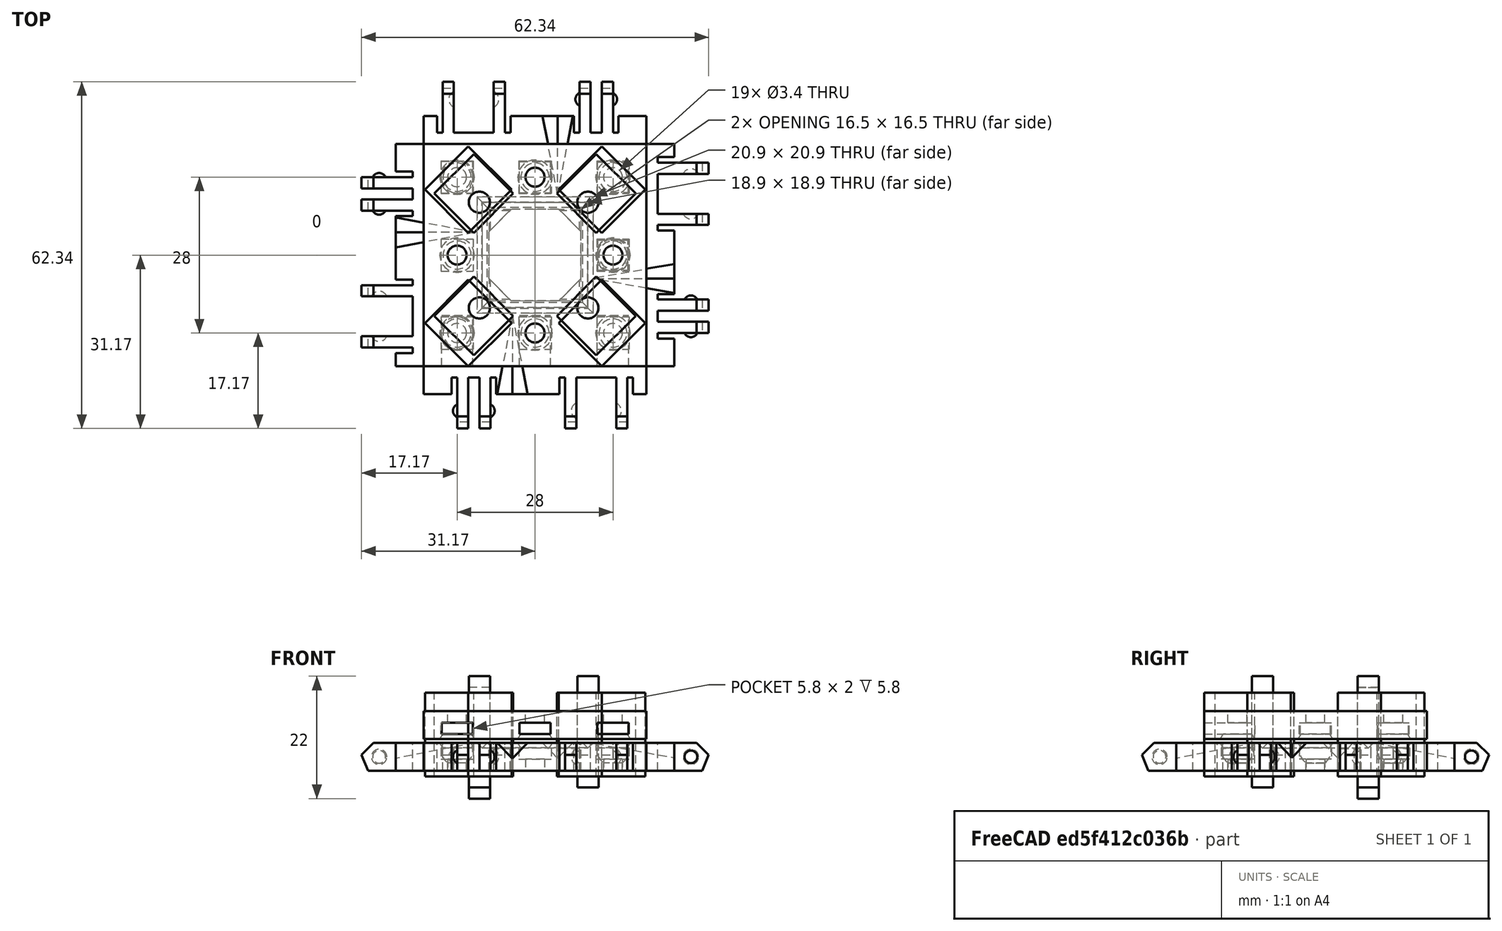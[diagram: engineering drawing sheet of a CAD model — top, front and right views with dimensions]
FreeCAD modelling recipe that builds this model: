
FCSTD DOCUMENT  (FreeCAD 0.17R13522 (Git))
Label: Robot Plates 0.4
License: All rights reserved
LicenseURL: http://en.wikipedia.org/wiki/All_rights_reserved
objects: Part::Box×147, Part::Sphere×51, Part::MultiFuse×49, Part::Cut×48, Part::Cylinder×27, Part::Chamfer×12, Part::Mirroring×2, Part::Fuse×2, App::DocumentObjectGroup×1, Drawing::FeatureViewAnnotation×1, Drawing::FeaturePage×1
note: 338 computed .brp shape members not serialized (recipe doc carries the construction recipe); baked Part::Feature solids carry a one-line shape summary decoded from their .brp

FEATURE [Part::Box] Box  label="Cube"
  AttacherType = Attacher::AttachEngine3D
  Height = 5
  Length = 40
  Placement = pos=(0,0,-2) rot=(0,0,1;0rad)
  Width = 40
FEATURE [Part::Sphere] Sphere003  label="Mag Hole 3"
  Angle1 = -90
  Angle2 = 90
  Angle3 = 360
  AttacherType = Attacher::AttachEngine3D
  Placement = pos=(6,34,1.7) rot=(0,0,1;0rad)
  Radius = 2.85
FEATURE [Part::Sphere] Sphere005  label="Mag Hole 2"
  Angle1 = -90
  Angle2 = 90
  Angle3 = 360
  AttacherType = Attacher::AttachEngine3D
  Placement = pos=(34,20,1.7) rot=(0,0,1;0rad)
  Radius = 2.85
FEATURE [Part::Sphere] Sphere  label="Mag Hole"
  Angle1 = -90
  Angle2 = 90
  Angle3 = 360
  AttacherType = Attacher::AttachEngine3D
  Placement = pos=(6,6,1.7) rot=(0,0,1;0rad)
  Radius = 2.85
FEATURE [Part::MultiFuse] Fusion004
  Shapes = -> [Sphere,Sphere005,Sphere003]
FEATURE [Part::Cut] Cut003
  Base = -> Box
  Tool = -> Fusion004
FEATURE [Part::Box] Box001  label="Cube001"
  AttacherType = Attacher::AttachEngine3D
  Height = 7
  Length = 5
  Width = 40
FEATURE [Part::Box] Box002  label="Cube002"
  AttacherType = Attacher::AttachEngine3D
  Height = 7
  Length = 10
  Placement = pos=(-10,6,0) rot=(0,0,1;0rad)
  Width = 2
FEATURE [Part::Box] Box003  label="Cube003"
  AttacherType = Attacher::AttachEngine3D
  Height = 7
  Length = 10
  Placement = pos=(-10,10,0) rot=(0,0,1;0rad)
  Width = 2
FEATURE [Part::Box] Box004  label="Cube004"
  AttacherType = Attacher::AttachEngine3D
  Height = 7
  Length = 10
  Placement = pos=(-10,25.4,0) rot=(0,0,1;0rad)
  Width = 2
FEATURE [Part::Box] Box005  label="Cube005"
  AttacherType = Attacher::AttachEngine3D
  Height = 7
  Length = 10
  Placement = pos=(-10,34.6,0) rot=(0,0,1;0rad)
  Width = 2
FEATURE [Part::Sphere] Sphere008
  Angle1 = -90
  Angle2 = 90
  Angle3 = 360
  AttacherType = Attacher::AttachEngine3D
  Placement = pos=(-3,6.5,2.5) rot=(0,0,1;0rad)
  Radius = 1.25
FEATURE [Part::Box] Box006  label="Cube006"
  AttacherType = Attacher::AttachEngine3D
  Height = 10
  Length = 13
  Placement = pos=(-10.19,0,-1.19) rot=(0,-1,0;0.785398rad)
  Width = 40
FEATURE [Part::Sphere] Sphere009
  Angle1 = -90
  Angle2 = 90
  Angle3 = 360
  AttacherType = Attacher::AttachEngine3D
  Placement = pos=(-3,11.5,2.5) rot=(0,0,1;0rad)
  Radius = 1.25
FEATURE [Part::Sphere] Sphere010
  Angle1 = -90
  Angle2 = 90
  Angle3 = 360
  AttacherType = Attacher::AttachEngine3D
  Placement = pos=(-3,28,2.5) rot=(0,0,1;0rad)
  Radius = 1.5
FEATURE [Part::Sphere] Sphere011
  Angle1 = -90
  Angle2 = 90
  Angle3 = 360
  AttacherType = Attacher::AttachEngine3D
  Placement = pos=(-3,34,2.5) rot=(0,0,1;0rad)
  Radius = 1.5
FEATURE [Part::MultiFuse] Fusion
  Shapes = -> [Box001,Box002,Box003,Box004,Box005]
FEATURE [Part::Cut] Cut
  Base = -> Fusion
  Tool = -> Box006
FEATURE [Part::MultiFuse] Fusion001
  Shapes = -> [Sphere008,Sphere009,Cut]
FEATURE [Part::MultiFuse] Fusion002
  Shapes = -> [Sphere011,Sphere010]
FEATURE [Part::Cut] Cut001
  Base = -> Fusion001
  Tool = -> Fusion002
FEATURE [Part::Chamfer] Chamfer001
  Base = -> Cut001
  Edges = 4 edges r=4: [Edge31,Edge37,Edge43,Edge46]
FEATURE [Part::Box] Box007  label="Cube007"
  AttacherType = Attacher::AttachEngine3D
  Height = 7
  Length = 4
  Placement = pos=(-1,5,0) rot=(0,0,1;0rad)
  Width = 1
FEATURE [Part::Box] Box008  label="Cube008"
  AttacherType = Attacher::AttachEngine3D
  Height = 7
  Length = 4
  Placement = pos=(-1,8,0) rot=(0,0,1;0rad)
  Width = 2
FEATURE [Part::Box] Box009  label="Cube009"
  AttacherType = Attacher::AttachEngine3D
  Height = 7
  Length = 4
  Placement = pos=(-1,12,0) rot=(0,0,1;0rad)
  Width = 1
FEATURE [Part::Box] Box010  label="Cube010"
  AttacherType = Attacher::AttachEngine3D
  Height = 7
  Length = 4
  Placement = pos=(-1,24.4,0) rot=(0,0,1;0rad)
  Width = 1
FEATURE [Part::Box] Box011  label="Cube011"
  AttacherType = Attacher::AttachEngine3D
  Height = 7
  Length = 4
  Placement = pos=(-1,36.6,0) rot=(0,0,1;0rad)
  Width = 1
FEATURE [Part::Box] Box012  label="Cube012"
  AttacherType = Attacher::AttachEngine3D
  Height = 7
  Length = 4
  Placement = pos=(-1,27.4,0) rot=(0,0,1;0rad)
  Width = 7.2
FEATURE [Part::MultiFuse] Fusion003
  Shapes = -> [Box012,Box009,Box011,Box008,Box010,Box007]
FEATURE [Part::Cut] Cut002
  Base = -> Chamfer001
  Placement = pos=(-5,40,3) rot=(1,0,0;3.14159rad)
  Tool = -> Fusion003
FEATURE [Part::Box] Box013  label="Cube013"
  AttacherType = Attacher::AttachEngine3D
  Height = 10
  Length = 12
  Placement = pos=(-11,-2,-12) rot=(0,0,1;0rad)
  Width = 44
FEATURE [Part::Cut] Cut004
  Base = -> Cut002
  Tool = -> Box013
FEATURE [Part::Box] Box014  label="Cube014"
  AttacherType = Attacher::AttachEngine3D
  Height = 7
  Length = 10
  Placement = pos=(-10,34.6,0) rot=(0,0,1;0rad)
  Width = 2
FEATURE [Part::Box] Box015  label="Cube015"
  AttacherType = Attacher::AttachEngine3D
  Height = 7
  Length = 5
  Width = 40
FEATURE [Part::Box] Box016  label="Cube016"
  AttacherType = Attacher::AttachEngine3D
  Height = 7
  Length = 10
  Placement = pos=(-10,25.4,0) rot=(0,0,1;0rad)
  Width = 2
FEATURE [Part::Box] Box017  label="Cube017"
  AttacherType = Attacher::AttachEngine3D
  Height = 7
  Length = 10
  Placement = pos=(-10,10,0) rot=(0,0,1;0rad)
  Width = 2
FEATURE [Part::Box] Box018  label="Cube018"
  AttacherType = Attacher::AttachEngine3D
  Height = 7
  Length = 10
  Placement = pos=(-10,6,0) rot=(0,0,1;0rad)
  Width = 2
FEATURE [Part::Sphere] Sphere012
  Angle1 = -90
  Angle2 = 90
  Angle3 = 360
  AttacherType = Attacher::AttachEngine3D
  Placement = pos=(-3,6.5,2.5) rot=(0,0,1;0rad)
  Radius = 1.25
FEATURE [Part::Box] Box019  label="Cube019"
  AttacherType = Attacher::AttachEngine3D
  Height = 10
  Length = 13
  Placement = pos=(-10.19,0,-1.19) rot=(0,-1,0;0.785398rad)
  Width = 40
FEATURE [Part::Sphere] Sphere013
  Angle1 = -90
  Angle2 = 90
  Angle3 = 360
  AttacherType = Attacher::AttachEngine3D
  Placement = pos=(-3,11.5,2.5) rot=(0,0,1;0rad)
  Radius = 1.25
FEATURE [Part::Sphere] Sphere014
  Angle1 = -90
  Angle2 = 90
  Angle3 = 360
  AttacherType = Attacher::AttachEngine3D
  Placement = pos=(-3,28,2.5) rot=(0,0,1;0rad)
  Radius = 1.5
FEATURE [Part::Sphere] Sphere015
  Angle1 = -90
  Angle2 = 90
  Angle3 = 360
  AttacherType = Attacher::AttachEngine3D
  Placement = pos=(-3,34,2.5) rot=(0,0,1;0rad)
  Radius = 1.5
FEATURE [Part::MultiFuse] Fusion005
  Shapes = -> [Box015,Box018,Box017,Box016,Box014]
FEATURE [Part::Cut] Cut005
  Base = -> Fusion005
  Tool = -> Box019
FEATURE [Part::MultiFuse] Fusion006
  Shapes = -> [Sphere012,Sphere013,Cut005]
FEATURE [Part::MultiFuse] Fusion007
  Shapes = -> [Sphere015,Sphere014]
FEATURE [Part::Cut] Cut006
  Base = -> Fusion006
  Tool = -> Fusion007
FEATURE [Part::Chamfer] Chamfer002
  Base = -> Cut006
  Edges = 4 edges r=4: [Edge31,Edge37,Edge43,Edge46]
FEATURE [Part::Box] Box020  label="Cube020"
  AttacherType = Attacher::AttachEngine3D
  Height = 7
  Length = 4
  Placement = pos=(-1,5,0) rot=(0,0,1;0rad)
  Width = 1
FEATURE [Part::Box] Box021  label="Cube021"
  AttacherType = Attacher::AttachEngine3D
  Height = 7
  Length = 4
  Placement = pos=(-1,8,0) rot=(0,0,1;0rad)
  Width = 2
FEATURE [Part::Box] Box022  label="Cube022"
  AttacherType = Attacher::AttachEngine3D
  Height = 7
  Length = 4
  Placement = pos=(-1,12,0) rot=(0,0,1;0rad)
  Width = 1
FEATURE [Part::Box] Box023  label="Cube023"
  AttacherType = Attacher::AttachEngine3D
  Height = 7
  Length = 4
  Placement = pos=(-1,24.4,0) rot=(0,0,1;0rad)
  Width = 1
FEATURE [Part::Box] Box024  label="Cube024"
  AttacherType = Attacher::AttachEngine3D
  Height = 7
  Length = 4
  Placement = pos=(-1,36.6,0) rot=(0,0,1;0rad)
  Width = 1
FEATURE [Part::Box] Box025  label="Cube025"
  AttacherType = Attacher::AttachEngine3D
  Height = 7
  Length = 4
  Placement = pos=(-1,27.4,0) rot=(0,0,1;0rad)
  Width = 7.2
FEATURE [Part::MultiFuse] Fusion008
  Shapes = -> [Box025,Box022,Box024,Box021,Box023,Box020]
FEATURE [Part::Cut] Cut007
  Base = -> Chamfer002
  Placement = pos=(-5,40,3) rot=(1,0,0;3.14159rad)
  Tool = -> Fusion008
FEATURE [Part::Box] Box026  label="Cube026"
  AttacherType = Attacher::AttachEngine3D
  Height = 10
  Length = 12
  Placement = pos=(-11,-2,-12) rot=(0,0,1;0rad)
  Width = 44
FEATURE [Part::Cut] Cut008
  Base = -> Cut007
  Placement = pos=(40,0,0) rot=(0,0,1;1.5708rad)
  Tool = -> Box026
FEATURE [Part::Box] Box027  label="Cube027"
  AttacherType = Attacher::AttachEngine3D
  Height = 7
  Length = 4
  Placement = pos=(-1,12,0) rot=(0,0,1;0rad)
  Width = 1
FEATURE [Part::Box] Box028  label="Cube028"
  AttacherType = Attacher::AttachEngine3D
  Height = 10
  Length = 13
  Placement = pos=(-10.19,0,-1.19) rot=(0,-1,0;0.785398rad)
  Width = 40
FEATURE [Part::Box] Box029  label="Cube029"
  AttacherType = Attacher::AttachEngine3D
  Height = 7
  Length = 4
  Placement = pos=(-1,27.4,0) rot=(0,0,1;0rad)
  Width = 7.2
FEATURE [Part::Box] Box030  label="Cube030"
  AttacherType = Attacher::AttachEngine3D
  Height = 7
  Length = 4
  Placement = pos=(-1,5,0) rot=(0,0,1;0rad)
  Width = 1
FEATURE [Part::Box] Box031  label="Cube031"
  AttacherType = Attacher::AttachEngine3D
  Height = 7
  Length = 10
  Placement = pos=(-10,6,0) rot=(0,0,1;0rad)
  Width = 2
FEATURE [Part::Box] Box032  label="Cube032"
  AttacherType = Attacher::AttachEngine3D
  Height = 10
  Length = 12
  Placement = pos=(-11,-2,-12) rot=(0,0,1;0rad)
  Width = 44
FEATURE [Part::Sphere] Sphere016
  Angle1 = -90
  Angle2 = 90
  Angle3 = 360
  AttacherType = Attacher::AttachEngine3D
  Placement = pos=(-3,6.5,2.5) rot=(0,0,1;0rad)
  Radius = 1.25
FEATURE [Part::Box] Box033  label="Cube033"
  AttacherType = Attacher::AttachEngine3D
  Height = 7
  Length = 10
  Placement = pos=(-10,25.4,0) rot=(0,0,1;0rad)
  Width = 2
FEATURE [Part::Box] Box034  label="Cube034"
  AttacherType = Attacher::AttachEngine3D
  Height = 7
  Length = 10
  Placement = pos=(-10,10,0) rot=(0,0,1;0rad)
  Width = 2
FEATURE [Part::Sphere] Sphere017
  Angle1 = -90
  Angle2 = 90
  Angle3 = 360
  AttacherType = Attacher::AttachEngine3D
  Placement = pos=(-3,28,2.5) rot=(0,0,1;0rad)
  Radius = 1.5
FEATURE [Part::Sphere] Sphere018
  Angle1 = -90
  Angle2 = 90
  Angle3 = 360
  AttacherType = Attacher::AttachEngine3D
  Placement = pos=(-3,11.5,2.5) rot=(0,0,1;0rad)
  Radius = 1.25
FEATURE [Part::Box] Box035  label="Cube035"
  AttacherType = Attacher::AttachEngine3D
  Height = 7
  Length = 4
  Placement = pos=(-1,36.6,0) rot=(0,0,1;0rad)
  Width = 1
FEATURE [Part::Sphere] Sphere019
  Angle1 = -90
  Angle2 = 90
  Angle3 = 360
  AttacherType = Attacher::AttachEngine3D
  Placement = pos=(-3,34,2.5) rot=(0,0,1;0rad)
  Radius = 1.5
FEATURE [Part::MultiFuse] Fusion011
  Shapes = -> [Sphere019,Sphere017]
FEATURE [Part::Box] Box036  label="Cube036"
  AttacherType = Attacher::AttachEngine3D
  Height = 7
  Length = 4
  Placement = pos=(-1,8,0) rot=(0,0,1;0rad)
  Width = 2
FEATURE [Part::Box] Box037  label="Cube037"
  AttacherType = Attacher::AttachEngine3D
  Height = 7
  Length = 10
  Placement = pos=(-10,34.6,0) rot=(0,0,1;0rad)
  Width = 2
FEATURE [Part::Box] Box038  label="Cube038"
  AttacherType = Attacher::AttachEngine3D
  Height = 7
  Length = 4
  Placement = pos=(-1,24.4,0) rot=(0,0,1;0rad)
  Width = 1
FEATURE [Part::MultiFuse] Fusion009
  Shapes = -> [Box029,Box027,Box035,Box036,Box038,Box030]
FEATURE [Part::Box] Box039  label="Cube039"
  AttacherType = Attacher::AttachEngine3D
  Height = 7
  Length = 5
  Width = 40
FEATURE [Part::MultiFuse] Fusion012
  Shapes = -> [Box039,Box031,Box034,Box033,Box037]
FEATURE [Part::Cut] Cut011
  Base = -> Fusion012
  Tool = -> Box028
FEATURE [Part::MultiFuse] Fusion010
  Shapes = -> [Sphere016,Sphere018,Cut011]
FEATURE [Part::Cut] Cut012
  Base = -> Fusion010
  Tool = -> Fusion011
FEATURE [Part::Chamfer] Chamfer003
  Base = -> Cut012
  Edges = 4 edges r=4: [Edge31,Edge37,Edge43,Edge46]
FEATURE [Part::Cut] Cut010
  Base = -> Chamfer003
  Placement = pos=(-5,40,3) rot=(1,0,0;3.14159rad)
  Tool = -> Fusion009
FEATURE [Part::Cut] Cut009
  Base = -> Cut010
  Placement = pos=(40,40,0) rot=(0,0,1;3.14159rad)
  Tool = -> Box032
FEATURE [Part::Sphere] Sphere020
  Angle1 = -90
  Angle2 = 90
  Angle3 = 360
  AttacherType = Attacher::AttachEngine3D
  Placement = pos=(-3,11.5,2.5) rot=(0,0,1;0rad)
  Radius = 1.25
FEATURE [Part::Box] Box040  label="Cube040"
  AttacherType = Attacher::AttachEngine3D
  Height = 7
  Length = 10
  Placement = pos=(-10,6,0) rot=(0,0,1;0rad)
  Width = 2
FEATURE [Part::Box] Box041  label="Cube041"
  AttacherType = Attacher::AttachEngine3D
  Height = 7
  Length = 4
  Placement = pos=(-1,8,0) rot=(0,0,1;0rad)
  Width = 2
FEATURE [Part::Box] Box042  label="Cube042"
  AttacherType = Attacher::AttachEngine3D
  Height = 7
  Length = 10
  Placement = pos=(-10,10,0) rot=(0,0,1;0rad)
  Width = 2
FEATURE [Part::Box] Box043  label="Cube043"
  AttacherType = Attacher::AttachEngine3D
  Height = 10
  Length = 12
  Placement = pos=(-11,-2,-12) rot=(0,0,1;0rad)
  Width = 44
FEATURE [Part::Box] Box044  label="Cube044"
  AttacherType = Attacher::AttachEngine3D
  Height = 7
  Length = 4
  Placement = pos=(-1,5,0) rot=(0,0,1;0rad)
  Width = 1
FEATURE [Part::Sphere] Sphere021
  Angle1 = -90
  Angle2 = 90
  Angle3 = 360
  AttacherType = Attacher::AttachEngine3D
  Placement = pos=(-3,28,2.5) rot=(0,0,1;0rad)
  Radius = 1.5
FEATURE [Part::Sphere] Sphere022
  Angle1 = -90
  Angle2 = 90
  Angle3 = 360
  AttacherType = Attacher::AttachEngine3D
  Placement = pos=(-3,6.5,2.5) rot=(0,0,1;0rad)
  Radius = 1.25
FEATURE [Part::Sphere] Sphere023
  Angle1 = -90
  Angle2 = 90
  Angle3 = 360
  AttacherType = Attacher::AttachEngine3D
  Placement = pos=(-3,34,2.5) rot=(0,0,1;0rad)
  Radius = 1.5
FEATURE [Part::Box] Box045  label="Cube045"
  AttacherType = Attacher::AttachEngine3D
  Height = 7
  Length = 4
  Placement = pos=(-1,12,0) rot=(0,0,1;0rad)
  Width = 1
FEATURE [Part::Box] Box046  label="Cube046"
  AttacherType = Attacher::AttachEngine3D
  Height = 7
  Length = 5
  Width = 40
FEATURE [Part::Box] Box047  label="Cube047"
  AttacherType = Attacher::AttachEngine3D
  Height = 7
  Length = 4
  Placement = pos=(-1,36.6,0) rot=(0,0,1;0rad)
  Width = 1
FEATURE [Part::Box] Box048  label="Cube048"
  AttacherType = Attacher::AttachEngine3D
  Height = 7
  Length = 4
  Placement = pos=(-1,24.4,0) rot=(0,0,1;0rad)
  Width = 1
FEATURE [Part::Box] Box049  label="Cube049"
  AttacherType = Attacher::AttachEngine3D
  Height = 7
  Length = 10
  Placement = pos=(-10,25.4,0) rot=(0,0,1;0rad)
  Width = 2
FEATURE [Part::Box] Box050  label="Cube050"
  AttacherType = Attacher::AttachEngine3D
  Height = 10
  Length = 13
  Placement = pos=(-10.19,0,-1.19) rot=(0,-1,0;0.785398rad)
  Width = 40
FEATURE [Part::Box] Box051  label="Cube051"
  AttacherType = Attacher::AttachEngine3D
  Height = 7
  Length = 10
  Placement = pos=(-10,34.6,0) rot=(0,0,1;0rad)
  Width = 2
FEATURE [Part::MultiFuse] Fusion015
  Shapes = -> [Box046,Box040,Box042,Box049,Box051]
FEATURE [Part::Cut] Cut013
  Base = -> Fusion015
  Tool = -> Box050
FEATURE [Part::MultiFuse] Fusion013
  Shapes = -> [Sphere022,Sphere020,Cut013]
FEATURE [Part::MultiFuse] Fusion016
  Shapes = -> [Sphere023,Sphere021]
FEATURE [Part::Cut] Cut014
  Base = -> Fusion013
  Tool = -> Fusion016
FEATURE [Part::Chamfer] Chamfer004
  Base = -> Cut014
  Edges = 4 edges r=4: [Edge31,Edge37,Edge43,Edge46]
FEATURE [Part::Box] Box052  label="Cube052"
  AttacherType = Attacher::AttachEngine3D
  Height = 7
  Length = 4
  Placement = pos=(-1,27.4,0) rot=(0,0,1;0rad)
  Width = 7.2
FEATURE [Part::MultiFuse] Fusion014
  Shapes = -> [Box052,Box045,Box047,Box041,Box048,Box044]
FEATURE [Part::Cut] Cut016
  Base = -> Chamfer004
  Placement = pos=(-5,40,3) rot=(1,0,0;3.14159rad)
  Tool = -> Fusion014
FEATURE [Part::Cut] Cut015
  Base = -> Cut016
  Placement = pos=(0,40,0) rot=(0,0,-1;1.5708rad)
  Tool = -> Box043
FEATURE [Part::Box] Box054  label="Cube054"
  AttacherType = Attacher::AttachEngine3D
  Height = 15
  Length = 10
  Placement = pos=(9,2,-3) rot=(0,0,1;0.785398rad)
  Width = 10
FEATURE [Part::Box] Box055  label="Cube055"
  AttacherType = Attacher::AttachEngine3D
  Height = 15
  Length = 10
  Placement = pos=(31,24,-3) rot=(0,0,1;0.785398rad)
  Width = 10
FEATURE [Part::Box] Box056  label="Cube056"
  AttacherType = Attacher::AttachEngine3D
  Height = 15
  Length = 10
  Placement = pos=(31,2,-3) rot=(0,0,1;0.785398rad)
  Width = 10
FEATURE [Part::Box] Box057  label="Cube057"
  AttacherType = Attacher::AttachEngine3D
  Height = 15
  Length = 10
  Placement = pos=(9,24,-3) rot=(0,0,1;0.785398rad)
  Width = 10
FEATURE [Part::MultiFuse] Fusion017
  Shapes = -> [Box054,Box057,Box056,Box055]
FEATURE [Part::Box] Box058  label="Cube058"
  AttacherType = Attacher::AttachEngine3D
  Height = 5
  Length = 40
  Placement = pos=(0,0,3.7) rot=(0,0,1;0rad)
  Width = 40
FEATURE [Part::Box] Box059  label="Square Nut Hole 008"
  AttacherType = Attacher::AttachEngine3D
  Height = 2
  Length = 5.6
  Placement = pos=(17.2,31.2,4.6) rot=(0,0,1;0rad)
  Width = 5.6
FEATURE [Part::Box] Box060  label="Square Nut Hole 009"
  AttacherType = Attacher::AttachEngine3D
  Height = 2
  Length = 5.6
  Placement = pos=(17.2,-0.85,4.6) rot=(0,0,1;0rad)
  Width = 10
FEATURE [Part::Box] Box061  label="Square Nut Hole 010"
  AttacherType = Attacher::AttachEngine3D
  Height = 2
  Length = 5.6
  Placement = pos=(31.2,-0.85,4.6) rot=(0,0,1;0rad)
  Width = 10
FEATURE [Part::Box] Box062  label="Square Nut Hole 011"
  AttacherType = Attacher::AttachEngine3D
  Height = 2
  Length = 5.4
  Placement = pos=(31.3,17.3,4.6) rot=(0,0,1;0rad)
  Width = 5.4
FEATURE [Part::Box] Box063  label="Square Nut Hole 012"
  AttacherType = Attacher::AttachEngine3D
  Height = 2
  Length = 5.7
  Placement = pos=(3.15,31.15,4.6) rot=(0,0,1;0rad)
  Width = 5.7
FEATURE [Part::Box] Box064  label="Square Nut Hole 013"
  AttacherType = Attacher::AttachEngine3D
  Height = 2
  Length = 5.5
  Placement = pos=(31.25,31.25,4.6) rot=(0,0,1;0rad)
  Width = 5.5
FEATURE [Part::Box] Box065  label="Square Nut Hole 014"
  AttacherType = Attacher::AttachEngine3D
  Height = 2
  Length = 5.8
  Placement = pos=(3.1,17.1,4.6) rot=(0,0,1;0rad)
  Width = 5.8
FEATURE [Part::Box] Box066  label="Square Nut Hole 015"
  AttacherType = Attacher::AttachEngine3D
  Height = 2
  Length = 5.6
  Placement = pos=(3.2,-0.85,4.6) rot=(0,0,1;0rad)
  Width = 10
FEATURE [Part::Sphere] Sphere006  label="Nut Clearence1"
  Angle1 = -90
  Angle2 = 90
  Angle3 = 360
  AttacherType = Attacher::AttachEngine3D
  Placement = pos=(6,6,2.4) rot=(0,0,1;0rad)
  Radius = 3.35
FEATURE [Part::Sphere] Sphere024
  Angle1 = -90
  Angle2 = 90
  Angle3 = 360
  AttacherType = Attacher::AttachEngine3D
  Placement = pos=(6,34,2.4) rot=(0,0,1;0rad)
  Radius = 3.35
FEATURE [Part::Sphere] Sphere007
  Angle1 = -90
  Angle2 = 90
  Angle3 = 360
  AttacherType = Attacher::AttachEngine3D
  Placement = pos=(34,20,2.4) rot=(0,0,1;0rad)
  Radius = 3.35
FEATURE [Part::Sphere] Sphere001
  Angle1 = -90
  Angle2 = 90
  Angle3 = 360
  AttacherType = Attacher::AttachEngine3D
  Placement = pos=(34,6,2.4) rot=(0,0,1;0rad)
  Radius = 3.35
FEATURE [Part::Sphere] Sphere025
  Angle1 = -90
  Angle2 = 90
  Angle3 = 360
  AttacherType = Attacher::AttachEngine3D
  Placement = pos=(20,6,2.4) rot=(0,0,1;0rad)
  Radius = 3.35
FEATURE [Part::Sphere] Sphere026
  Angle1 = -90
  Angle2 = 90
  Angle3 = 360
  AttacherType = Attacher::AttachEngine3D
  Placement = pos=(20,34,2.4) rot=(0,0,1;0rad)
  Radius = 3.35
FEATURE [Part::Sphere] Sphere004
  Angle1 = -90
  Angle2 = 90
  Angle3 = 360
  AttacherType = Attacher::AttachEngine3D
  Placement = pos=(6,20,2.4) rot=(0,0,1;0rad)
  Radius = 3.35
FEATURE [Part::Sphere] Sphere002
  Angle1 = -90
  Angle2 = 90
  Angle3 = 360
  AttacherType = Attacher::AttachEngine3D
  Placement = pos=(34,34,2.4) rot=(0,0,1;0rad)
  Radius = 3.35
FEATURE [Part::Cylinder] Cylinder
  Angle = 360
  AttacherType = Attacher::AttachEngine3D
  Height = 10
  Placement = pos=(6,6,0) rot=(0,0,1;0rad)
  Radius = 1.7
FEATURE [Part::Cylinder] Cylinder002
  Angle = 360
  AttacherType = Attacher::AttachEngine3D
  Height = 10
  Placement = pos=(34,6,0) rot=(0,0,1;0rad)
  Radius = 1.7
FEATURE [Part::Cylinder] Cylinder001
  Angle = 360
  AttacherType = Attacher::AttachEngine3D
  Height = 10
  Placement = pos=(20,6,0) rot=(0,0,1;0rad)
  Radius = 1.7
FEATURE [Part::Cylinder] Cylinder003
  Angle = 360
  AttacherType = Attacher::AttachEngine3D
  Height = 10
  Placement = pos=(34,34,0) rot=(0,0,1;0rad)
  Radius = 1.7
FEATURE [Part::Cylinder] Cylinder004
  Angle = 360
  AttacherType = Attacher::AttachEngine3D
  Height = 10
  Placement = pos=(20,34,0) rot=(0,0,1;0rad)
  Radius = 1.7
FEATURE [Part::Cylinder] Cylinder005
  Angle = 360
  AttacherType = Attacher::AttachEngine3D
  Height = 10
  Placement = pos=(6,34,0) rot=(0,0,1;0rad)
  Radius = 1.7
FEATURE [Part::Cylinder] Cylinder006
  Angle = 360
  AttacherType = Attacher::AttachEngine3D
  Height = 10
  Placement = pos=(6,20,0) rot=(0,0,1;0rad)
  Radius = 1.7
FEATURE [Part::Cylinder] Cylinder007
  Angle = 360
  AttacherType = Attacher::AttachEngine3D
  Height = 10
  Placement = pos=(34,20,0) rot=(0,0,1;0rad)
  Radius = 1.7
FEATURE [Part::MultiFuse] Fusion018
  Shapes = -> [Cylinder,Cylinder004,Cylinder007,Cylinder005,Cylinder006,Cylinder001,Cylinder002,Cylinder003]
FEATURE [Part::MultiFuse] Fusion019
  Shapes = -> [Sphere007,Sphere024,Sphere006,Sphere025,Sphere001,Sphere026,Sphere004,Sphere002]
FEATURE [Part::MultiFuse] Fusion020
  Shapes = -> [Box061,Box065,Box062,Box063,Box064,Box066,Box059,Box060]
FEATURE [Part::Cut] Cut017
  Base = -> Box058
  Tool = -> Fusion020
FEATURE [Part::Cut] Cut019
  Base = -> Cut017
  Tool = -> Fusion019
FEATURE [Part::Cut] Cut018
  Base = -> Cut019
  Tool = -> Fusion018
FEATURE [Part::Cylinder] Cylinder008
  Angle = 360
  AttacherType = Attacher::AttachEngine3D
  Height = 20
  Placement = pos=(10,10.5,-5) rot=(0,0,1;0rad)
  Radius = 1.9
FEATURE [Part::Cylinder] Cylinder009
  Angle = 360
  AttacherType = Attacher::AttachEngine3D
  Height = 20
  Placement = pos=(29.5,10.5,-5) rot=(0,0,1;0rad)
  Radius = 1.9
FEATURE [Part::Cylinder] Cylinder010
  Angle = 360
  AttacherType = Attacher::AttachEngine3D
  Height = 20
  Placement = pos=(29.5,29.5,-5) rot=(0,0,1;0rad)
  Radius = 1.9
FEATURE [Part::Cylinder] Cylinder011
  Angle = 360
  AttacherType = Attacher::AttachEngine3D
  Height = 20
  Placement = pos=(10,29.5,-7) rot=(0,0,1;0rad)
  Radius = 1.9
FEATURE [Part::MultiFuse] Fusion021  label="M2 Screw holes"
  Shapes = -> [Cylinder008,Cylinder009,Cylinder011,Cylinder010]
FEATURE [Part::Box] Box067  label="Square Nut Hole 016"
  AttacherType = Attacher::AttachEngine3D
  Height = 2
  Length = 5.8
  Placement = pos=(31.1,17.1,4.6) rot=(0,0,1;0rad)
  Width = 5.8
FEATURE [Part::Box] Box068  label="Square Nut Hole 017"
  AttacherType = Attacher::AttachEngine3D
  Height = 2
  Length = 5.8
  Placement = pos=(17.1,3.1,4.6) rot=(0,0,1;0rad)
  Width = 5.8
FEATURE [Part::Box] Box069  label="Square Nut Hole 018"
  AttacherType = Attacher::AttachEngine3D
  Height = 2
  Length = 5.8
  Placement = pos=(31.1,3.1,4.6) rot=(0,0,1;0rad)
  Width = 5.8
FEATURE [Part::Box] Box070  label="Square Nut Hole 019"
  AttacherType = Attacher::AttachEngine3D
  Height = 2
  Length = 5.8
  Placement = pos=(3.1,3.1,4.6) rot=(0,0,1;0rad)
  Width = 5.8
FEATURE [Part::Box] Box071  label="Square Nut Hole 020"
  AttacherType = Attacher::AttachEngine3D
  Height = 2
  Length = 5.8
  Placement = pos=(3.1,31.1,4.6) rot=(0,0,1;0rad)
  Width = 5.8
FEATURE [Part::Box] Box072  label="Square Nut Hole 021"
  AttacherType = Attacher::AttachEngine3D
  Height = 2
  Length = 5.8
  Placement = pos=(17.1,31.1,4.6) rot=(0,0,1;0rad)
  Width = 5.8
FEATURE [Part::Box] Box073  label="Square Nut Hole 022"
  AttacherType = Attacher::AttachEngine3D
  Height = 2
  Length = 5.8
  Placement = pos=(31.1,31.1,4.6) rot=(0,0,1;0rad)
  Width = 5.8
FEATURE [Part::Box] Box074  label="Square Nut Hole 023"
  AttacherType = Attacher::AttachEngine3D
  Height = 2
  Length = 5.8
  Placement = pos=(3.1,17.1,4.6) rot=(0,0,1;0rad)
  Width = 5.8
FEATURE [Part::Cylinder] Cylinder012
  Angle = 360
  AttacherType = Attacher::AttachEngine3D
  Height = 10
  Placement = pos=(6,6,0) rot=(0,0,1;0rad)
  Radius = 1.7
FEATURE [Part::Cylinder] Cylinder013
  Angle = 360
  AttacherType = Attacher::AttachEngine3D
  Height = 10
  Placement = pos=(34,34,0) rot=(0,0,1;0rad)
  Radius = 1.7
FEATURE [Part::Cylinder] Cylinder014
  Angle = 360
  AttacherType = Attacher::AttachEngine3D
  Height = 10
  Placement = pos=(20,34,0) rot=(0,0,1;0rad)
  Radius = 1.7
FEATURE [Part::Cylinder] Cylinder015
  Angle = 360
  AttacherType = Attacher::AttachEngine3D
  Height = 10
  Placement = pos=(6,34,0) rot=(0,0,1;0rad)
  Radius = 1.7
FEATURE [Part::Cylinder] Cylinder016
  Angle = 360
  AttacherType = Attacher::AttachEngine3D
  Height = 10
  Placement = pos=(6,20,0) rot=(0,0,1;0rad)
  Radius = 1.7
FEATURE [Part::Cylinder] Cylinder017
  Angle = 360
  AttacherType = Attacher::AttachEngine3D
  Height = 10
  Placement = pos=(34,20,0) rot=(0,0,1;0rad)
  Radius = 1.7
FEATURE [Part::Cylinder] Cylinder018
  Angle = 360
  AttacherType = Attacher::AttachEngine3D
  Height = 10
  Placement = pos=(34,6,0) rot=(0,0,1;0rad)
  Radius = 1.7
FEATURE [Part::Cylinder] Cylinder019
  Angle = 360
  AttacherType = Attacher::AttachEngine3D
  Height = 10
  Placement = pos=(20,6,0) rot=(0,0,1;0rad)
  Radius = 1.7
FEATURE [Part::Box] Box075  label="Cube059"
  AttacherType = Attacher::AttachEngine3D
  Height = 5
  Length = 40
  Placement = pos=(0,0,-2) rot=(0,0,1;0rad)
  Width = 40
FEATURE [Part::Sphere] Sphere027
  Angle1 = -90
  Angle2 = 90
  Angle3 = 360
  AttacherType = Attacher::AttachEngine3D
  Placement = pos=(34,20,2.4) rot=(0,0,1;0rad)
  Radius = 3.35
FEATURE [Part::Sphere] Sphere028  label="Nut Clearence002"
  Angle1 = -90
  Angle2 = 90
  Angle3 = 360
  AttacherType = Attacher::AttachEngine3D
  Placement = pos=(6,6,2.4) rot=(0,0,1;0rad)
  Radius = 3.35
FEATURE [Part::Sphere] Sphere029
  Angle1 = -90
  Angle2 = 90
  Angle3 = 360
  AttacherType = Attacher::AttachEngine3D
  Placement = pos=(34,34,2.4) rot=(0,0,1;0rad)
  Radius = 3.35
FEATURE [Part::Sphere] Sphere030
  Angle1 = -90
  Angle2 = 90
  Angle3 = 360
  AttacherType = Attacher::AttachEngine3D
  Placement = pos=(34,6,2.4) rot=(0,0,1;0rad)
  Radius = 3.35
FEATURE [Part::Sphere] Sphere031
  Angle1 = -90
  Angle2 = 90
  Angle3 = 360
  AttacherType = Attacher::AttachEngine3D
  Placement = pos=(20,6,2.4) rot=(0,0,1;0rad)
  Radius = 3.35
FEATURE [Part::Sphere] Sphere032
  Angle1 = -90
  Angle2 = 90
  Angle3 = 360
  AttacherType = Attacher::AttachEngine3D
  Placement = pos=(6,34,2.4) rot=(0,0,1;0rad)
  Radius = 3.35
FEATURE [Part::Sphere] Sphere033
  Angle1 = -90
  Angle2 = 90
  Angle3 = 360
  AttacherType = Attacher::AttachEngine3D
  Placement = pos=(6,20,2.4) rot=(0,0,1;0rad)
  Radius = 3.35
FEATURE [Part::Sphere] Sphere034
  Angle1 = -90
  Angle2 = 90
  Angle3 = 360
  AttacherType = Attacher::AttachEngine3D
  Placement = pos=(20,34,2.4) rot=(0,0,1;0rad)
  Radius = 3.35
FEATURE [Part::Box] Box076  label="Cube060"
  AttacherType = Attacher::AttachEngine3D
  Height = 15
  Length = 16.5
  Placement = pos=(11.75,11.75,-3) rot=(0,0,1;0rad)
  Width = 16.5
FEATURE [Part::Box] Box077  label="Cube061"
  AttacherType = Attacher::AttachEngine3D
  Height = 15
  Length = 11
  Placement = pos=(8,24,-3) rot=(0,0,1;0.785398rad)
  Width = 11
FEATURE [Part::Box] Box078  label="Cube062"
  AttacherType = Attacher::AttachEngine3D
  Height = 15
  Length = 11
  Placement = pos=(8,0,-3) rot=(0,0,1;0.785398rad)
  Width = 11
FEATURE [Part::Box] Box079  label="Cube063"
  AttacherType = Attacher::AttachEngine3D
  Height = 15
  Length = 11
  Placement = pos=(32,0,-3) rot=(0,0,1;0.785398rad)
  Width = 11
FEATURE [Part::Box] Box080  label="Cube064"
  AttacherType = Attacher::AttachEngine3D
  Height = 15
  Length = 11
  Placement = pos=(32,24,-3) rot=(0,0,1;0.785398rad)
  Width = 11
FEATURE [Part::MultiFuse] Fusion022
  Shapes = -> [Box078,Box077,Box079,Box080]
FEATURE [Part::Cylinder] Cylinder020
  Angle = 360
  AttacherType = Attacher::AttachEngine3D
  Height = 20
  Placement = pos=(29.5,10.5,-5) rot=(0,0,1;0rad)
  Radius = 1.9
FEATURE [Part::Cylinder] Cylinder021
  Angle = 360
  AttacherType = Attacher::AttachEngine3D
  Height = 20
  Placement = pos=(10,29.5,-7) rot=(0,0,1;0rad)
  Radius = 1.9
FEATURE [Part::Cylinder] Cylinder022
  Angle = 360
  AttacherType = Attacher::AttachEngine3D
  Height = 20
  Placement = pos=(10,10.5,-5) rot=(0,0,1;0rad)
  Radius = 1.9
FEATURE [Part::Cylinder] Cylinder023
  Angle = 360
  AttacherType = Attacher::AttachEngine3D
  Height = 20
  Placement = pos=(29.5,29.5,-5) rot=(0,0,1;0rad)
  Radius = 1.9
FEATURE [Part::MultiFuse] Fusion023  label="M2 Screw holes001"
  Shapes = -> [Cylinder022,Cylinder020,Cylinder021,Cylinder023]
FEATURE [Part::MultiFuse] Fusion024  label="Square Nut Hole"
  Shapes = -> [Box067,Box073,Box071,Box069,Box068,Box070,Box072,Box074]
FEATURE [Part::MultiFuse] Fusion025  label="Square Nut Screw Holes"
  Shapes = -> [Cylinder012,Cylinder018,Cylinder016,Cylinder015,Cylinder014,Cylinder013,Cylinder017,Cylinder019]
FEATURE [Part::MultiFuse] Fusion026  label="Nut Chamfers"
  Shapes = -> [Sphere027,Sphere028,Sphere029,Sphere031,Sphere032,Sphere033,Sphere034,Sphere030]
FEATURE [App::DocumentObjectGroup] Group  label="Cubes"
  Group = -> [Fusion017,Fusion022]
FEATURE [Part::Box] Box082  label="Cube066"
  AttacherType = Attacher::AttachEngine3D
  Height = 10
  Length = 15
  Placement = pos=(30.8481,15.8,2.86019) rot=(0.974848,0.205904,-0.085288;0.803573rad)
  Width = 10
FEATURE [Part::Box] Box083  label="Cube067"
  AttacherType = Attacher::AttachEngine3D
  Height = 10
  Length = 21
  Placement = pos=(9.5,9.5,2.1) rot=(0,0,1;0rad)
  Width = 21
FEATURE [Part::Box] Box084  label="Cube068"
  AttacherType = Attacher::AttachEngine3D
  Height = 14
  Length = 17
  Placement = pos=(11.5,11.5,0) rot=(0,0,1;0rad)
  Width = 17
FEATURE [Part::Cut] Cut020
  Base = -> Box083
  Tool = -> Box084
FEATURE [Part::Chamfer] Chamfer007
  Base = -> Cut020
  Edges = 8 edges r=0.95: [Edge4,Edge5,Edge14,Edge16,Edge17,Edge18,Edge19,Edge20]
FEATURE [Part::Chamfer] Chamfer008
  Base = -> Box076
  Edges = 4 edges r=4: [Edge1,Edge3,Edge5,Edge7]
FEATURE [Part::Box] Box085  label="Cube069"
  AttacherType = Attacher::AttachEngine3D
  Height = 15
  Length = 16
  Placement = pos=(12,12,-13) rot=(0,0,1;0rad)
  Width = 16
FEATURE [Part::Box] Box086  label="Cube070"
  AttacherType = Attacher::AttachEngine3D
  Height = 10
  Length = 10
  Placement = pos=(17,32.0919,9.95) rot=(-0.225436,0.969773,-0.093378;0.807337rad)
  Width = 15
FEATURE [Part::Box] Box087  label="Cube071"
  AttacherType = Attacher::AttachEngine3D
  Height = 10
  Length = 10
  Placement = pos=(7.9081,17,9.95) rot=(-0.450607,0.280623,0.847469;1.65638rad)
  Width = 15
FEATURE [Part::Box] Box088  label="Cube072"
  AttacherType = Attacher::AttachEngine3D
  Height = 10
  Length = 10
  Placement = pos=(23,7.9081,9.95) rot=(-0.381178,-0.08861,0.920245;3.06822rad)
  Width = 15
FEATURE [Part::MultiFuse] Fusion027
  Shapes = -> [Box086,Box082,Box087,Box088]
FEATURE [Part::MultiFuse] Fusion028
  Shapes = -> [Cut015,Cut004,Cut008,Cut009]
FEATURE [Part::Box] Box089  label="Cube073"
  AttacherType = Attacher::AttachEngine3D
  Height = 10
  Length = 10
  Placement = pos=(17,32.0919,9.95) rot=(-0.225436,0.969773,-0.093378;0.807337rad)
  Width = 15
FEATURE [Part::Box] Box090  label="Cube074"
  AttacherType = Attacher::AttachEngine3D
  Height = 10
  Length = 15
  Placement = pos=(30.8481,15.8,2.86019) rot=(0.974848,0.205904,-0.085288;0.803573rad)
  Width = 10
FEATURE [Part::Box] Box091  label="Cube075"
  AttacherType = Attacher::AttachEngine3D
  Height = 10
  Length = 10
  Placement = pos=(7.9081,17,9.95) rot=(-0.450607,0.280623,0.847469;1.65638rad)
  Width = 15
FEATURE [Part::Box] Box092  label="Cube076"
  AttacherType = Attacher::AttachEngine3D
  Height = 10
  Length = 10
  Placement = pos=(23,7.9081,9.95) rot=(-0.381178,-0.08861,0.920245;3.06822rad)
  Width = 15
FEATURE [Part::Box] Box093  label="Cube077"
  AttacherType = Attacher::AttachEngine3D
  Height = 7
  Length = 5
  Width = 40
FEATURE [Part::Box] Box094  label="Cube078"
  AttacherType = Attacher::AttachEngine3D
  Height = 7
  Length = 10
  Placement = pos=(-10,6,0) rot=(0,0,1;0rad)
  Width = 2
FEATURE [Part::Box] Box095  label="Cube079"
  AttacherType = Attacher::AttachEngine3D
  Height = 7
  Length = 10
  Placement = pos=(-10,10,0) rot=(0,0,1;0rad)
  Width = 2
FEATURE [Part::Box] Box096  label="Cube080"
  AttacherType = Attacher::AttachEngine3D
  Height = 7
  Length = 10
  Placement = pos=(-10,25.4,0) rot=(0,0,1;0rad)
  Width = 2
FEATURE [Part::Box] Box097  label="Cube081"
  AttacherType = Attacher::AttachEngine3D
  Height = 7
  Length = 10
  Placement = pos=(-10,34.6,0) rot=(0,0,1;0rad)
  Width = 2
FEATURE [Part::Sphere] Sphere035
  Angle1 = -90
  Angle2 = 90
  Angle3 = 360
  AttacherType = Attacher::AttachEngine3D
  Placement = pos=(-3,6.5,2.5) rot=(0,0,1;0rad)
  Radius = 1.25
FEATURE [Part::Box] Box098  label="Cube082"
  AttacherType = Attacher::AttachEngine3D
  Height = 10
  Length = 13
  Placement = pos=(-10.19,0,-1.19) rot=(0,-1,0;0.785398rad)
  Width = 40
FEATURE [Part::Sphere] Sphere036
  Angle1 = -90
  Angle2 = 90
  Angle3 = 360
  AttacherType = Attacher::AttachEngine3D
  Placement = pos=(-3,11.5,2.5) rot=(0,0,1;0rad)
  Radius = 1.25
FEATURE [Part::Sphere] Sphere037
  Angle1 = -90
  Angle2 = 90
  Angle3 = 360
  AttacherType = Attacher::AttachEngine3D
  Placement = pos=(-3,28,2.5) rot=(0,0,1;0rad)
  Radius = 1.5
FEATURE [Part::Sphere] Sphere038
  Angle1 = -90
  Angle2 = 90
  Angle3 = 360
  AttacherType = Attacher::AttachEngine3D
  Placement = pos=(-3,34,2.5) rot=(0,0,1;0rad)
  Radius = 1.5
FEATURE [Part::MultiFuse] Fusion030
  Shapes = -> [Box093,Box094,Box095,Box096,Box097]
FEATURE [Part::Cut] Cut025
  Base = -> Fusion030
  Tool = -> Box098
FEATURE [Part::MultiFuse] Fusion031
  Shapes = -> [Sphere035,Sphere036,Cut025]
FEATURE [Part::MultiFuse] Fusion032
  Shapes = -> [Sphere038,Sphere037]
FEATURE [Part::Cut] Cut026
  Base = -> Fusion031
  Tool = -> Fusion032
FEATURE [Part::Chamfer] Chamfer009
  Base = -> Cut026
  Edges = 4 edges r=4: [Edge31,Edge37,Edge43,Edge46]
FEATURE [Part::Box] Box099  label="Cube083"
  AttacherType = Attacher::AttachEngine3D
  Height = 7
  Length = 4
  Placement = pos=(-1,5,0) rot=(0,0,1;0rad)
  Width = 1
FEATURE [Part::Box] Box100  label="Cube084"
  AttacherType = Attacher::AttachEngine3D
  Height = 7
  Length = 4
  Placement = pos=(-1,8,0) rot=(0,0,1;0rad)
  Width = 2
FEATURE [Part::Box] Box101  label="Cube085"
  AttacherType = Attacher::AttachEngine3D
  Height = 7
  Length = 4
  Placement = pos=(-1,12,0) rot=(0,0,1;0rad)
  Width = 1
FEATURE [Part::Box] Box102  label="Cube086"
  AttacherType = Attacher::AttachEngine3D
  Height = 7
  Length = 4
  Placement = pos=(-1,24.4,0) rot=(0,0,1;0rad)
  Width = 1
FEATURE [Part::Box] Box103  label="Cube087"
  AttacherType = Attacher::AttachEngine3D
  Height = 7
  Length = 4
  Placement = pos=(-1,36.6,0) rot=(0,0,1;0rad)
  Width = 1
FEATURE [Part::Box] Box104  label="Cube088"
  AttacherType = Attacher::AttachEngine3D
  Height = 7
  Length = 4
  Placement = pos=(-1,27.4,0) rot=(0,0,1;0rad)
  Width = 7.2
FEATURE [Part::MultiFuse] Fusion033
  Shapes = -> [Box104,Box101,Box103,Box100,Box102,Box099]
FEATURE [Part::Cut] Cut027
  Base = -> Chamfer009
  Placement = pos=(-5,40,3) rot=(1,0,0;3.14159rad)
  Tool = -> Fusion033
FEATURE [Part::Box] Box105  label="Cube089"
  AttacherType = Attacher::AttachEngine3D
  Height = 10
  Length = 12
  Placement = pos=(-11,-2,-12) rot=(0,0,1;0rad)
  Width = 44
FEATURE [Part::Cut] Cut028
  Base = -> Cut027
  Tool = -> Box105
FEATURE [Part::Box] Box106  label="Cube090"
  AttacherType = Attacher::AttachEngine3D
  Height = 7
  Length = 10
  Placement = pos=(-10,34.6,0) rot=(0,0,1;0rad)
  Width = 2
FEATURE [Part::Box] Box107  label="Cube091"
  AttacherType = Attacher::AttachEngine3D
  Height = 7
  Length = 5
  Width = 40
FEATURE [Part::Box] Box108  label="Cube092"
  AttacherType = Attacher::AttachEngine3D
  Height = 7
  Length = 10
  Placement = pos=(-10,25.4,0) rot=(0,0,1;0rad)
  Width = 2
FEATURE [Part::Box] Box109  label="Cube093"
  AttacherType = Attacher::AttachEngine3D
  Height = 7
  Length = 10
  Placement = pos=(-10,10,0) rot=(0,0,1;0rad)
  Width = 2
FEATURE [Part::Box] Box110  label="Cube094"
  AttacherType = Attacher::AttachEngine3D
  Height = 7
  Length = 10
  Placement = pos=(-10,6,0) rot=(0,0,1;0rad)
  Width = 2
FEATURE [Part::Sphere] Sphere039
  Angle1 = -90
  Angle2 = 90
  Angle3 = 360
  AttacherType = Attacher::AttachEngine3D
  Placement = pos=(-3,6.5,2.5) rot=(0,0,1;0rad)
  Radius = 1.25
FEATURE [Part::Box] Box111  label="Cube095"
  AttacherType = Attacher::AttachEngine3D
  Height = 10
  Length = 13
  Placement = pos=(-10.19,0,-1.19) rot=(0,-1,0;0.785398rad)
  Width = 40
FEATURE [Part::Sphere] Sphere040
  Angle1 = -90
  Angle2 = 90
  Angle3 = 360
  AttacherType = Attacher::AttachEngine3D
  Placement = pos=(-3,11.5,2.5) rot=(0,0,1;0rad)
  Radius = 1.25
FEATURE [Part::Sphere] Sphere041
  Angle1 = -90
  Angle2 = 90
  Angle3 = 360
  AttacherType = Attacher::AttachEngine3D
  Placement = pos=(-3,28,2.5) rot=(0,0,1;0rad)
  Radius = 1.5
FEATURE [Part::Sphere] Sphere042
  Angle1 = -90
  Angle2 = 90
  Angle3 = 360
  AttacherType = Attacher::AttachEngine3D
  Placement = pos=(-3,34,2.5) rot=(0,0,1;0rad)
  Radius = 1.5
FEATURE [Part::MultiFuse] Fusion034
  Shapes = -> [Box107,Box110,Box109,Box108,Box106]
FEATURE [Part::Cut] Cut029
  Base = -> Fusion034
  Tool = -> Box111
FEATURE [Part::MultiFuse] Fusion035
  Shapes = -> [Sphere039,Sphere040,Cut029]
FEATURE [Part::MultiFuse] Fusion036
  Shapes = -> [Sphere042,Sphere041]
FEATURE [Part::Cut] Cut030
  Base = -> Fusion035
  Tool = -> Fusion036
FEATURE [Part::Chamfer] Chamfer010
  Base = -> Cut030
  Edges = 4 edges r=4: [Edge31,Edge37,Edge43,Edge46]
FEATURE [Part::Box] Box112  label="Cube096"
  AttacherType = Attacher::AttachEngine3D
  Height = 7
  Length = 4
  Placement = pos=(-1,5,0) rot=(0,0,1;0rad)
  Width = 1
FEATURE [Part::Box] Box113  label="Cube097"
  AttacherType = Attacher::AttachEngine3D
  Height = 7
  Length = 4
  Placement = pos=(-1,8,0) rot=(0,0,1;0rad)
  Width = 2
FEATURE [Part::Box] Box114  label="Cube098"
  AttacherType = Attacher::AttachEngine3D
  Height = 7
  Length = 4
  Placement = pos=(-1,12,0) rot=(0,0,1;0rad)
  Width = 1
FEATURE [Part::Box] Box115  label="Cube099"
  AttacherType = Attacher::AttachEngine3D
  Height = 7
  Length = 4
  Placement = pos=(-1,24.4,0) rot=(0,0,1;0rad)
  Width = 1
FEATURE [Part::Box] Box116  label="Cube100"
  AttacherType = Attacher::AttachEngine3D
  Height = 7
  Length = 4
  Placement = pos=(-1,36.6,0) rot=(0,0,1;0rad)
  Width = 1
FEATURE [Part::Box] Box117  label="Cube101"
  AttacherType = Attacher::AttachEngine3D
  Height = 7
  Length = 4
  Placement = pos=(-1,27.4,0) rot=(0,0,1;0rad)
  Width = 7.2
FEATURE [Part::MultiFuse] Fusion037
  Shapes = -> [Box117,Box114,Box116,Box113,Box115,Box112]
FEATURE [Part::Cut] Cut031
  Base = -> Chamfer010
  Placement = pos=(-5,40,3) rot=(1,0,0;3.14159rad)
  Tool = -> Fusion037
FEATURE [Part::Box] Box118  label="Cube102"
  AttacherType = Attacher::AttachEngine3D
  Height = 10
  Length = 12
  Placement = pos=(-11,-2,-12) rot=(0,0,1;0rad)
  Width = 44
FEATURE [Part::Cut] Cut032
  Base = -> Cut031
  Placement = pos=(40,0,0) rot=(0,0,1;1.5708rad)
  Tool = -> Box118
FEATURE [Part::Box] Box119  label="Cube103"
  AttacherType = Attacher::AttachEngine3D
  Height = 7
  Length = 4
  Placement = pos=(-1,12,0) rot=(0,0,1;0rad)
  Width = 1
FEATURE [Part::Box] Box120  label="Cube104"
  AttacherType = Attacher::AttachEngine3D
  Height = 10
  Length = 13
  Placement = pos=(-10.19,0,-1.19) rot=(0,-1,0;0.785398rad)
  Width = 40
FEATURE [Part::Box] Box121  label="Cube105"
  AttacherType = Attacher::AttachEngine3D
  Height = 7
  Length = 4
  Placement = pos=(-1,27.4,0) rot=(0,0,1;0rad)
  Width = 7.2
FEATURE [Part::Box] Box122  label="Cube106"
  AttacherType = Attacher::AttachEngine3D
  Height = 7
  Length = 4
  Placement = pos=(-1,5,0) rot=(0,0,1;0rad)
  Width = 1
FEATURE [Part::Box] Box123  label="Cube107"
  AttacherType = Attacher::AttachEngine3D
  Height = 7
  Length = 10
  Placement = pos=(-10,6,0) rot=(0,0,1;0rad)
  Width = 2
FEATURE [Part::Box] Box124  label="Cube108"
  AttacherType = Attacher::AttachEngine3D
  Height = 10
  Length = 12
  Placement = pos=(-11,-2,-12) rot=(0,0,1;0rad)
  Width = 44
FEATURE [Part::Sphere] Sphere043
  Angle1 = -90
  Angle2 = 90
  Angle3 = 360
  AttacherType = Attacher::AttachEngine3D
  Placement = pos=(-3,6.5,2.5) rot=(0,0,1;0rad)
  Radius = 1.25
FEATURE [Part::Box] Box125  label="Cube109"
  AttacherType = Attacher::AttachEngine3D
  Height = 7
  Length = 10
  Placement = pos=(-10,25.4,0) rot=(0,0,1;0rad)
  Width = 2
FEATURE [Part::Box] Box126  label="Cube110"
  AttacherType = Attacher::AttachEngine3D
  Height = 7
  Length = 10
  Placement = pos=(-10,10,0) rot=(0,0,1;0rad)
  Width = 2
FEATURE [Part::Sphere] Sphere044
  Angle1 = -90
  Angle2 = 90
  Angle3 = 360
  AttacherType = Attacher::AttachEngine3D
  Placement = pos=(-3,28,2.5) rot=(0,0,1;0rad)
  Radius = 1.5
FEATURE [Part::Sphere] Sphere045
  Angle1 = -90
  Angle2 = 90
  Angle3 = 360
  AttacherType = Attacher::AttachEngine3D
  Placement = pos=(-3,11.5,2.5) rot=(0,0,1;0rad)
  Radius = 1.25
FEATURE [Part::Box] Box127  label="Cube111"
  AttacherType = Attacher::AttachEngine3D
  Height = 7
  Length = 4
  Placement = pos=(-1,36.6,0) rot=(0,0,1;0rad)
  Width = 1
FEATURE [Part::Sphere] Sphere046
  Angle1 = -90
  Angle2 = 90
  Angle3 = 360
  AttacherType = Attacher::AttachEngine3D
  Placement = pos=(-3,34,2.5) rot=(0,0,1;0rad)
  Radius = 1.5
FEATURE [Part::MultiFuse] Fusion040
  Shapes = -> [Sphere046,Sphere044]
FEATURE [Part::Box] Box128  label="Cube112"
  AttacherType = Attacher::AttachEngine3D
  Height = 7
  Length = 4
  Placement = pos=(-1,8,0) rot=(0,0,1;0rad)
  Width = 2
FEATURE [Part::Box] Box129  label="Cube113"
  AttacherType = Attacher::AttachEngine3D
  Height = 7
  Length = 10
  Placement = pos=(-10,34.6,0) rot=(0,0,1;0rad)
  Width = 2
FEATURE [Part::Box] Box130  label="Cube114"
  AttacherType = Attacher::AttachEngine3D
  Height = 7
  Length = 4
  Placement = pos=(-1,24.4,0) rot=(0,0,1;0rad)
  Width = 1
FEATURE [Part::MultiFuse] Fusion038
  Shapes = -> [Box121,Box119,Box127,Box128,Box130,Box122]
FEATURE [Part::Box] Box131  label="Cube115"
  AttacherType = Attacher::AttachEngine3D
  Height = 7
  Length = 5
  Width = 40
FEATURE [Part::MultiFuse] Fusion041
  Shapes = -> [Box131,Box123,Box126,Box125,Box129]
FEATURE [Part::Cut] Cut035
  Base = -> Fusion041
  Tool = -> Box120
FEATURE [Part::MultiFuse] Fusion039
  Shapes = -> [Sphere043,Sphere045,Cut035]
FEATURE [Part::Cut] Cut036
  Base = -> Fusion039
  Tool = -> Fusion040
FEATURE [Part::Chamfer] Chamfer011
  Base = -> Cut036
  Edges = 4 edges r=4: [Edge31,Edge37,Edge43,Edge46]
FEATURE [Part::Cut] Cut034
  Base = -> Chamfer011
  Placement = pos=(-5,40,3) rot=(1,0,0;3.14159rad)
  Tool = -> Fusion038
FEATURE [Part::Cut] Cut033
  Base = -> Cut034
  Placement = pos=(40,40,0) rot=(0,0,1;3.14159rad)
  Tool = -> Box124
FEATURE [Part::Sphere] Sphere047
  Angle1 = -90
  Angle2 = 90
  Angle3 = 360
  AttacherType = Attacher::AttachEngine3D
  Placement = pos=(-3,11.5,2.5) rot=(0,0,1;0rad)
  Radius = 1.25
FEATURE [Part::Box] Box132  label="Cube116"
  AttacherType = Attacher::AttachEngine3D
  Height = 7
  Length = 10
  Placement = pos=(-10,6,0) rot=(0,0,1;0rad)
  Width = 2
FEATURE [Part::Box] Box133  label="Cube117"
  AttacherType = Attacher::AttachEngine3D
  Height = 7
  Length = 4
  Placement = pos=(-1,8,0) rot=(0,0,1;0rad)
  Width = 2
FEATURE [Part::Box] Box134  label="Cube118"
  AttacherType = Attacher::AttachEngine3D
  Height = 7
  Length = 10
  Placement = pos=(-10,10,0) rot=(0,0,1;0rad)
  Width = 2
FEATURE [Part::Box] Box135  label="Cube119"
  AttacherType = Attacher::AttachEngine3D
  Height = 10
  Length = 12
  Placement = pos=(-11,-2,-12) rot=(0,0,1;0rad)
  Width = 44
FEATURE [Part::Box] Box136  label="Cube120"
  AttacherType = Attacher::AttachEngine3D
  Height = 7
  Length = 4
  Placement = pos=(-1,5,0) rot=(0,0,1;0rad)
  Width = 1
FEATURE [Part::Sphere] Sphere048
  Angle1 = -90
  Angle2 = 90
  Angle3 = 360
  AttacherType = Attacher::AttachEngine3D
  Placement = pos=(-3,28,2.5) rot=(0,0,1;0rad)
  Radius = 1.5
FEATURE [Part::Sphere] Sphere049
  Angle1 = -90
  Angle2 = 90
  Angle3 = 360
  AttacherType = Attacher::AttachEngine3D
  Placement = pos=(-3,6.5,2.5) rot=(0,0,1;0rad)
  Radius = 1.25
FEATURE [Part::Sphere] Sphere050
  Angle1 = -90
  Angle2 = 90
  Angle3 = 360
  AttacherType = Attacher::AttachEngine3D
  Placement = pos=(-3,34,2.5) rot=(0,0,1;0rad)
  Radius = 1.5
FEATURE [Part::Box] Box137  label="Cube121"
  AttacherType = Attacher::AttachEngine3D
  Height = 7
  Length = 4
  Placement = pos=(-1,12,0) rot=(0,0,1;0rad)
  Width = 1
FEATURE [Part::Box] Box138  label="Cube122"
  AttacherType = Attacher::AttachEngine3D
  Height = 7
  Length = 5
  Width = 40
FEATURE [Part::Box] Box139  label="Cube123"
  AttacherType = Attacher::AttachEngine3D
  Height = 7
  Length = 4
  Placement = pos=(-1,36.6,0) rot=(0,0,1;0rad)
  Width = 1
FEATURE [Part::Box] Box140  label="Cube124"
  AttacherType = Attacher::AttachEngine3D
  Height = 7
  Length = 4
  Placement = pos=(-1,24.4,0) rot=(0,0,1;0rad)
  Width = 1
FEATURE [Part::Box] Box141  label="Cube125"
  AttacherType = Attacher::AttachEngine3D
  Height = 7
  Length = 10
  Placement = pos=(-10,25.4,0) rot=(0,0,1;0rad)
  Width = 2
FEATURE [Part::Box] Box142  label="Cube126"
  AttacherType = Attacher::AttachEngine3D
  Height = 10
  Length = 13
  Placement = pos=(-10.19,0,-1.19) rot=(0,-1,0;0.785398rad)
  Width = 40
FEATURE [Part::Box] Box143  label="Cube127"
  AttacherType = Attacher::AttachEngine3D
  Height = 7
  Length = 10
  Placement = pos=(-10,34.6,0) rot=(0,0,1;0rad)
  Width = 2
FEATURE [Part::MultiFuse] Fusion044
  Shapes = -> [Box138,Box132,Box134,Box141,Box143]
FEATURE [Part::Cut] Cut037
  Base = -> Fusion044
  Tool = -> Box142
FEATURE [Part::MultiFuse] Fusion042
  Shapes = -> [Sphere049,Sphere047,Cut037]
FEATURE [Part::MultiFuse] Fusion045
  Shapes = -> [Sphere050,Sphere048]
FEATURE [Part::Cut] Cut038
  Base = -> Fusion042
  Tool = -> Fusion045
FEATURE [Part::Chamfer] Chamfer012
  Base = -> Cut038
  Edges = 4 edges r=4: [Edge31,Edge37,Edge43,Edge46]
FEATURE [Part::Box] Box144  label="Cube128"
  AttacherType = Attacher::AttachEngine3D
  Height = 7
  Length = 4
  Placement = pos=(-1,27.4,0) rot=(0,0,1;0rad)
  Width = 7.2
FEATURE [Part::MultiFuse] Fusion043
  Shapes = -> [Box144,Box137,Box139,Box133,Box140,Box136]
FEATURE [Part::Cut] Cut040
  Base = -> Chamfer012
  Placement = pos=(-5,40,3) rot=(1,0,0;3.14159rad)
  Tool = -> Fusion043
FEATURE [Part::Cut] Cut039
  Base = -> Cut040
  Placement = pos=(0,40,0) rot=(0,0,-1;1.5708rad)
  Tool = -> Box135
FEATURE [Part::MultiFuse] Fusion046
  Shapes = -> [Cut039,Cut028,Cut032,Cut033]
FEATURE [Part::MultiFuse] Fusion047
  Placement = pos=(0,40,6.7) rot=(1,0,0;3.14159rad)
  Shapes = -> [Fusion026,Fusion024,Fusion025]
FEATURE [Part::MultiFuse] Fusion048
  Shapes = -> [Box089,Box091,Box090,Box092]
FEATURE [Part::Box] Box145  label="Cube129"
  AttacherType = Attacher::AttachEngine3D
  Height = 15
  Length = 16
  Placement = pos=(12,12,-13) rot=(0,0,1;0rad)
  Width = 16
FEATURE [Part::Box] Box146  label="Cube130"
  AttacherType = Attacher::AttachEngine3D
  Height = 15
  Length = 16.5
  Placement = pos=(11.75,11.75,-3) rot=(0,0,1;0rad)
  Width = 16.5
FEATURE [Part::Chamfer] Chamfer013
  Base = -> Box146
  Edges = 4 edges r=4: [Edge1,Edge3,Edge5,Edge7]
FEATURE [Part::Box] Box147  label="Cube131"
  AttacherType = Attacher::AttachEngine3D
  Height = 10
  Length = 21
  Placement = pos=(9.5,9.5,2.1) rot=(0,0,1;0rad)
  Width = 21
FEATURE [Part::Box] Box148  label="Cube132"
  AttacherType = Attacher::AttachEngine3D
  Height = 14
  Length = 17
  Placement = pos=(11.5,11.5,0) rot=(0,0,1;0rad)
  Width = 17
FEATURE [Part::Cut] Cut043
  Base = -> Box147
  Tool = -> Box148
FEATURE [Part::Chamfer] Chamfer014
  Base = -> Cut043
  Edges = 8 edges r=0.95: [Edge4,Edge5,Edge14,Edge16,Edge17,Edge18,Edge19,Edge20]
FEATURE [Part::Cut] Cut047
  Base = -> Cut003
  Tool = -> Chamfer007
FEATURE [Part::Cut] Cut048
  Base = -> Cut047
  Tool = -> Chamfer008
FEATURE [Part::Cut] Cut049
  Base = -> Cut048
  Tool = -> Box085
FEATURE [Part::Mirroring] Part__Mirroring  label="Fusion028 (Mirror #1)"
  Base = (0,0,0)
  Normal = (0,0,1)
  Placement = pos=(0,0,1) rot=(0,0,1;0rad)
  Source = -> Fusion028
FEATURE [Part::Fuse] Fusion050
  Base = -> Cut049
  Tool = -> Part__Mirroring
FEATURE [Part::Cut] Cut050
  Base = -> Fusion050
  Tool = -> Fusion027
FEATURE [Part::Mirroring] Part__Mirroring001  label="Fusion046 (Mirror #2)"
  Base = (0,0,0)
  Normal = (0,0,1)
  Placement = pos=(0,0,1) rot=(0,0,1;0rad)
  Source = -> Fusion046
FEATURE [Part::Fuse] Fusion051
  Base = -> Box075
  Tool = -> Part__Mirroring001
FEATURE [Part::Cut] Cut051
  Base = -> Fusion051
  Tool = -> Fusion047
FEATURE [Part::Cut] Cut052
  Base = -> Cut051
  Tool = -> Fusion048
FEATURE [Part::Cut] Cut053
  Base = -> Cut052
  Tool = -> Chamfer014
FEATURE [Part::Cut] Cut054
  Base = -> Cut053
  Tool = -> Chamfer013
FEATURE [Part::Cut] Cut055
  Base = -> Cut054
  Tool = -> Box145
FEATURE [Part::Cylinder] Cylinder024
  Angle = 360
  AttacherType = Attacher::AttachEngine3D
  Height = 10
  Placement = pos=(6,6,-5) rot=(0,0,1;0rad)
  Radius = 1.7
FEATURE [Part::Cylinder] Cylinder025
  Angle = 360
  AttacherType = Attacher::AttachEngine3D
  Height = 10
  Placement = pos=(34,20,-5) rot=(0,0,1;0rad)
  Radius = 1.7
FEATURE [Part::Cylinder] Cylinder026
  Angle = 360
  AttacherType = Attacher::AttachEngine3D
  Height = 10
  Placement = pos=(6,34,-5) rot=(0,0,1;0rad)
  Radius = 1.7
FEATURE [Part::MultiFuse] Fusion052
  Shapes = -> [Cylinder024,Cylinder025,Cylinder026]
FEATURE [Part::Cut] Cut056
  Base = -> Cut050
  Tool = -> Fusion052
FEATURE [Drawing::FeatureViewAnnotation] Annotation
  Font = Sans
  Rotation = 0
  Scale = 7
  Text = Added in Holes to Mag plate for removal of magnet
  ViewResult = <g transform="translate(14,23) rotate(0)">\n<text id="Annotation"\n font-family="Sans"\n font-size="7"\n fill="#000000">\n<tspan x="0" dy="1em">Added in Holes to Mag plate for removal of magnet</tspan>\n</text>\n</g>
  Visible = true
  X = 14
  Y = 23
FEATURE [Drawing::FeaturePage] Page
  EditableTexts = AUTHOR NAME | CREATION DATE | SUPERVISOR NAME | CHECK DATE | SCALE | WEIGHT | NUMBER | SHEET | TITLE | SUBTITLE
  Group = -> [Annotation]
  Template = <path>
note: 1 file-system path scrubbed to <path> (originals preserved in the JSON sidecar)
